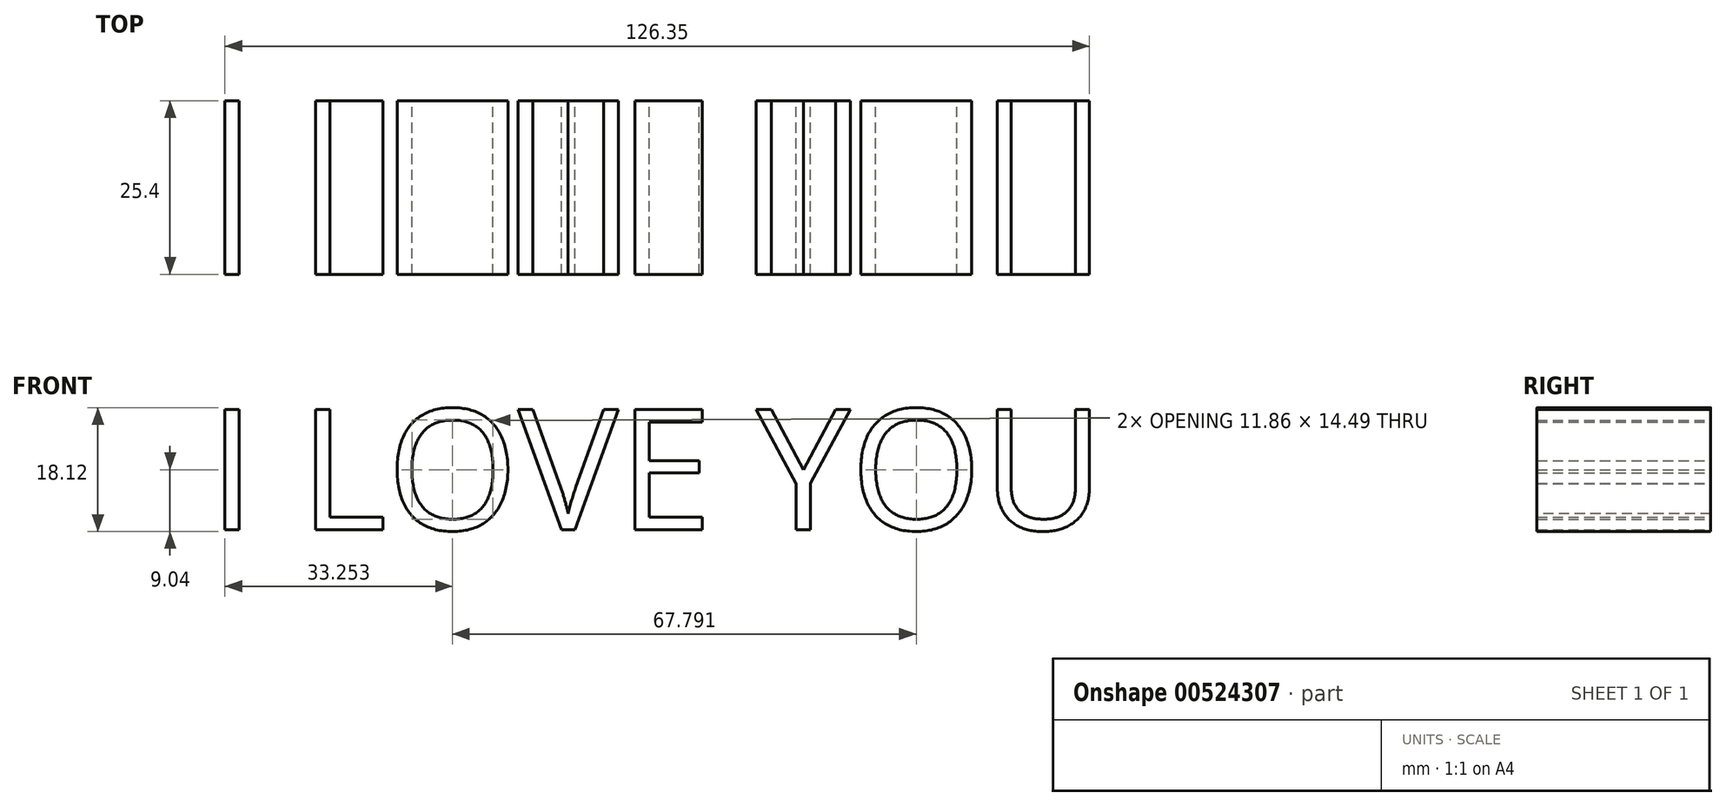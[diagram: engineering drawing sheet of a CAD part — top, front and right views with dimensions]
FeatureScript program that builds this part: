
annotation { "Feature Type Name" : "Feature", "Feature Type Description" : "" }
export const myFeature = defineFeature(function(context is Context, id is Id, definition is map)
    precondition{}
    {
        {
            var Q0;
            Q0=qCreatedBy(makeId("Front.planeOp"),FACE);
            var sketch = newSketch(context, id + "F0", { "sketchPlane" : qUnion([Q0])});
            skText(sketch, "E0", { "text": "I LOVE YOU\n", "fontName": "OpenSans-Regular.ttf"});
            const initialGuessF0  = {"E0": [-0.06898, 0.0308, 1, 0, 0.01775]};
            skSetInitialGuess(sketch, initialGuessF0);
            skSolve(sketch);
        }
        {
            var Q0;
            Q0 = qSketchRegion(id + "F0", true);
            extrude(context, id + "F1", {"entities" : qUnion([Q0]), "depth" : 25.4 * mm, "offsetDistance" : 25.4 * mm});
        }
    });
